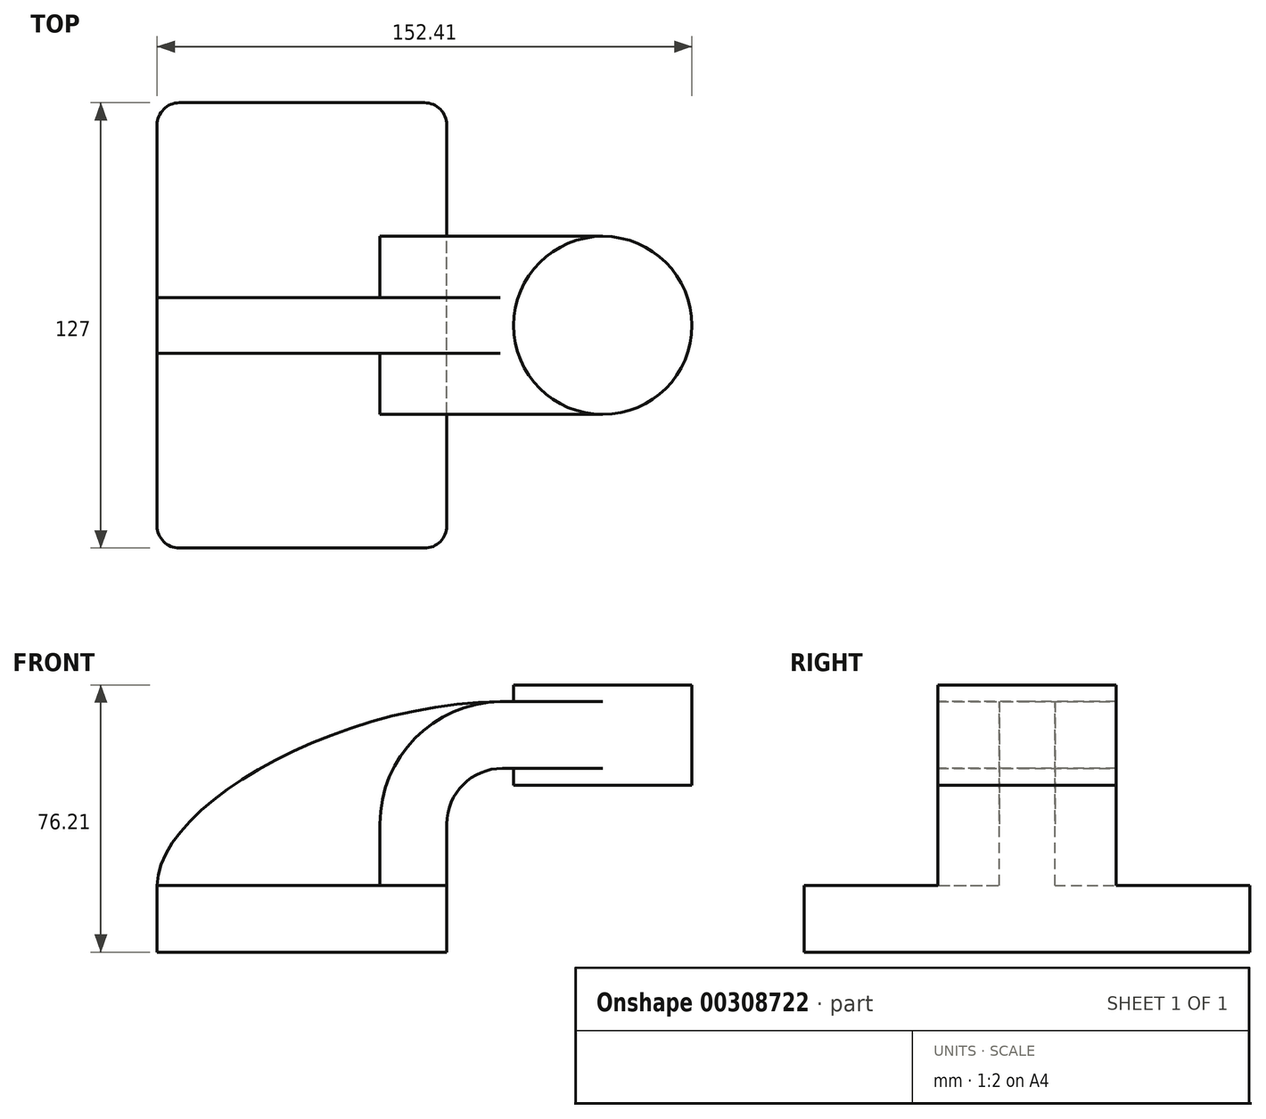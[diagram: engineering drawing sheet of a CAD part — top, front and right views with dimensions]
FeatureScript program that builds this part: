
annotation { "Feature Type Name" : "Feature", "Feature Type Description" : "" }
export const myFeature = defineFeature(function(context is Context, id is Id, definition is map)
    precondition{}
    {
        {
            var Q0;
            Q0=qCreatedBy(makeId("Front.planeOp"),FACE);
            var sketch = newSketch(context, id + "F0", { "sketchPlane" : qUnion([Q0])});
            skLineSegment(sketch, "E0.bottom", {"start": v(41.28, 9.52) * mm, "end": v(-41.28, 9.52) * mm});
            skLineSegment(sketch, "E0.top", {"start": v(41.28, -9.53) * mm, "end": v(-41.27, -9.53) * mm});
            skLineSegment(sketch, "E0.left", {"start": v(41.28, 9.52) * mm, "end": v(41.28, -9.53) * mm});
            skLineSegment(sketch, "E0.right", {"start": v(-41.28, 9.52) * mm, "end": v(-41.28, -9.53) * mm});
            skPoint(sketch, "E0.middle", {"position": v(0, 0) * mm});
            skLineSegment(sketch, "E1.bottom", {"start": v(111.12, 66.67) * mm, "end": v(60.32, 66.67) * mm});
            skLineSegment(sketch, "E1.top", {"start": v(111.12, 38.1) * mm, "end": v(60.33, 38.1) * mm});
            skLineSegment(sketch, "E1.left", {"start": v(111.12, 66.67) * mm, "end": v(111.12, 38.1) * mm});
            skLineSegment(sketch, "E1.right", {"start": v(60.32, 66.67) * mm, "end": v(60.33, 38.1) * mm});
            skPoint(sketch, "E1.middle", {"position": v(85.72, 52.39) * mm});
            skLineSegment(sketch, "E2", {"start": v(41.28, 9.52) * mm, "end": v(41.28, 27) * mm});
            skArc(sketch, "E3", {"start": v(41.27, 27) * mm, "mid": v(45.92, 38.23) * mm, "end": v(57.15, 42.88) * mm});
            skLineSegment(sketch, "E4", {"start": v(57.15, 42.88) * mm, "end": v(85.72, 42.88) * mm});
            skLineSegment(sketch, "E5.0", {"start": v(57.15, 61.93) * mm, "end": v(85.72, 61.93) * mm});
            skArc(sketch, "E5.1", {"start": v(22.22, 27) * mm, "mid": v(32.45, 51.7) * mm, "end": v(57.15, 61.93) * mm});
            skLineSegment(sketch, "E5.2", {"start": v(22.22, 9.52) * mm, "end": v(22.22, 27) * mm});
            skLineSegment(sketch, "E6", {"start": v(85.72, 38.1) * mm, "end": v(85.72, 66.67) * mm});
            skFitSpline(sketch, "E7", {"points": [v(-41.28, 9.52) * mm, v(57.15, 61.93) * mm], "startDerivative": vector(0.27, 67.28) * mm, "endDerivative": vector(142.14, 0.96) * mm});
            skSolve(sketch);
        }
        {
            var Q0;
            Q0=makeQuery(id+"F0.imprint","IMPRINT",FACE,{"disambiguationData":[TD([[makeQuery(id+"F0.imprint","IMPRINT",EDGE,{"derivedFrom":sQuery(id+"F0.wireOp",EDGE,"E0.top")}),-1.0]])]});
            extrude(context, id + "F1", {"entities" : qUnion([Q0]), "endBound" : BoundingType.SYMMETRIC, "depth" : 127 * mm});
        }
        {
            var Q0;
            {var subQ1=sQuery(id+"F0.wireOp",EDGE,"E2");Q0=makeQuery(id+"F0.imprint","IMPRINT",FACE,{"disambiguationData":[TD([[makeQuery(id+"F0.imprint","IMPRINT",EDGE,{"derivedFrom":subQ1}),1.0]])]});}
            var Q1;
            {var subQ0=sQuery(id+"F0.wireOp",EDGE,"E5.0");var subQ1=sQuery(id+"F0.wireOp",EDGE,"E1.right");var subQ2=makeQuery(id+"F0.imprint","INTERSECT",VERTEX,{"derivedFrom":[subQ1,subQ0]});Q1=makeQuery(id+"F0.imprint","IMPRINT",FACE,{"disambiguationData":[TD([[makeQuery(id+"F0.imprint","IMPRINT",EDGE,{"disambiguationData":[TD([[subQ2,-1.0]])],"derivedFrom":subQ1}),1.0]])]});}
            extrude(context, id + "F2", {"entities" : qUnion([Q0, Q1]), "operationType" : NewBodyOperationType.ADD, "endBound" : BoundingType.SYMMETRIC, "depth" : 50.8 * mm});
        }
        {
            var Q0;
            {var subQ3=sQuery(id+"F0.wireOp",EDGE,"E5.2");Q0=makeQuery(id+"F0.imprint","IMPRINT",FACE,{"disambiguationData":[TD([[makeQuery(id+"F0.imprint","IMPRINT",EDGE,{"derivedFrom":subQ3}),1.0]])]});}
            extrude(context, id + "F3", {"entities" : qUnion([Q0]), "operationType" : NewBodyOperationType.ADD, "endBound" : BoundingType.SYMMETRIC, "depth" : 15.88 * mm});
        }
        {
            var Q0;
            {var subQ0=sQuery(id+"F0.wireOp",EDGE,"E1.left");Q0=makeQuery(id+"F0.imprint","IMPRINT",FACE,{"disambiguationData":[TD([[makeQuery(id+"F0.imprint","IMPRINT",EDGE,{"derivedFrom":subQ0}),-1.0]])]});}
            var Q1;
            Q1=sQuery(id+"F0.wireOp",EDGE,"E6");
            revolve(context, id + "F4", {"operationType" : NewBodyOperationType.ADD, "entities" : qUnion([Q0]), "axis" : qUnion([Q1]), "revolveType" : RevolveType.FULL});
        }
        {
            var Q0;
            Q0=makeQuery(id+"F1.opExtrude","CAP_EDGE",EDGE,{"disambiguationData":[OSD([sQuery(id+"F0.wireOp",EDGE,"E0.left")])],"isStart":true});
            var Q1;
            Q1=makeQuery(id+"F1.opExtrude","CAP_EDGE",EDGE,{"disambiguationData":[OSD([sQuery(id+"F0.wireOp",EDGE,"E0.right")])],"isStart":true});
            var Q2;
            Q2=makeQuery(id+"F1.opExtrude","CAP_EDGE",EDGE,{"disambiguationData":[OSD([sQuery(id+"F0.wireOp",EDGE,"E0.left")])],"isStart":false});
            var Q3;
            Q3=makeQuery(id+"F1.opExtrude","CAP_EDGE",EDGE,{"disambiguationData":[OSD([sQuery(id+"F0.wireOp",EDGE,"E0.right")])],"isStart":false});
            fillet(context, id + "F5", {"entities" : qUnion([Q0, Q1, Q2, Q3]), "radius" : 6.35 * mm, "tangentPropagation" : true, "allowEdgeOverflow" : false});
        }
    });
